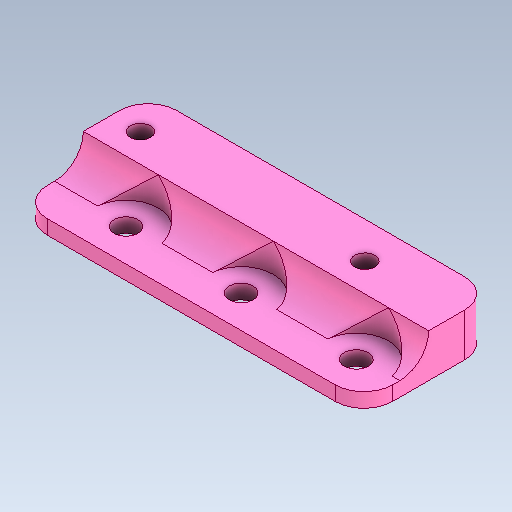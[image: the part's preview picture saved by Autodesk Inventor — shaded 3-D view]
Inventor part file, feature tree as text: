
AUTODESK INVENTOR PART (.ipt)
format: ipt  version: 2023 (Build 270158000, 158)  size: 173,056 bytes
history: native  units: in
note: dims shown in document units (in); Inventor stores cm internally (conversion verified against a paired STEP export)
features: sketch x4, other x3
ambient origin geometry x8: Origin, YZ Plane, XZ Plane, XY Plane, X Axis, Y Axis, Z Axis, Center Point
bodies: Solid1 (feature_tree)
feature tree (7):
  other  "DriveMotorMount5.ipt"
  other  "Solid1::DriveMotorMount5.ipt"
  other  "TaggingFeature1"
  sketch  "Sketch1"  dims[d0=0.3937in]
  sketch  "Sketch2"
  sketch  "Sketch3"
  sketch  "Sketch4"
